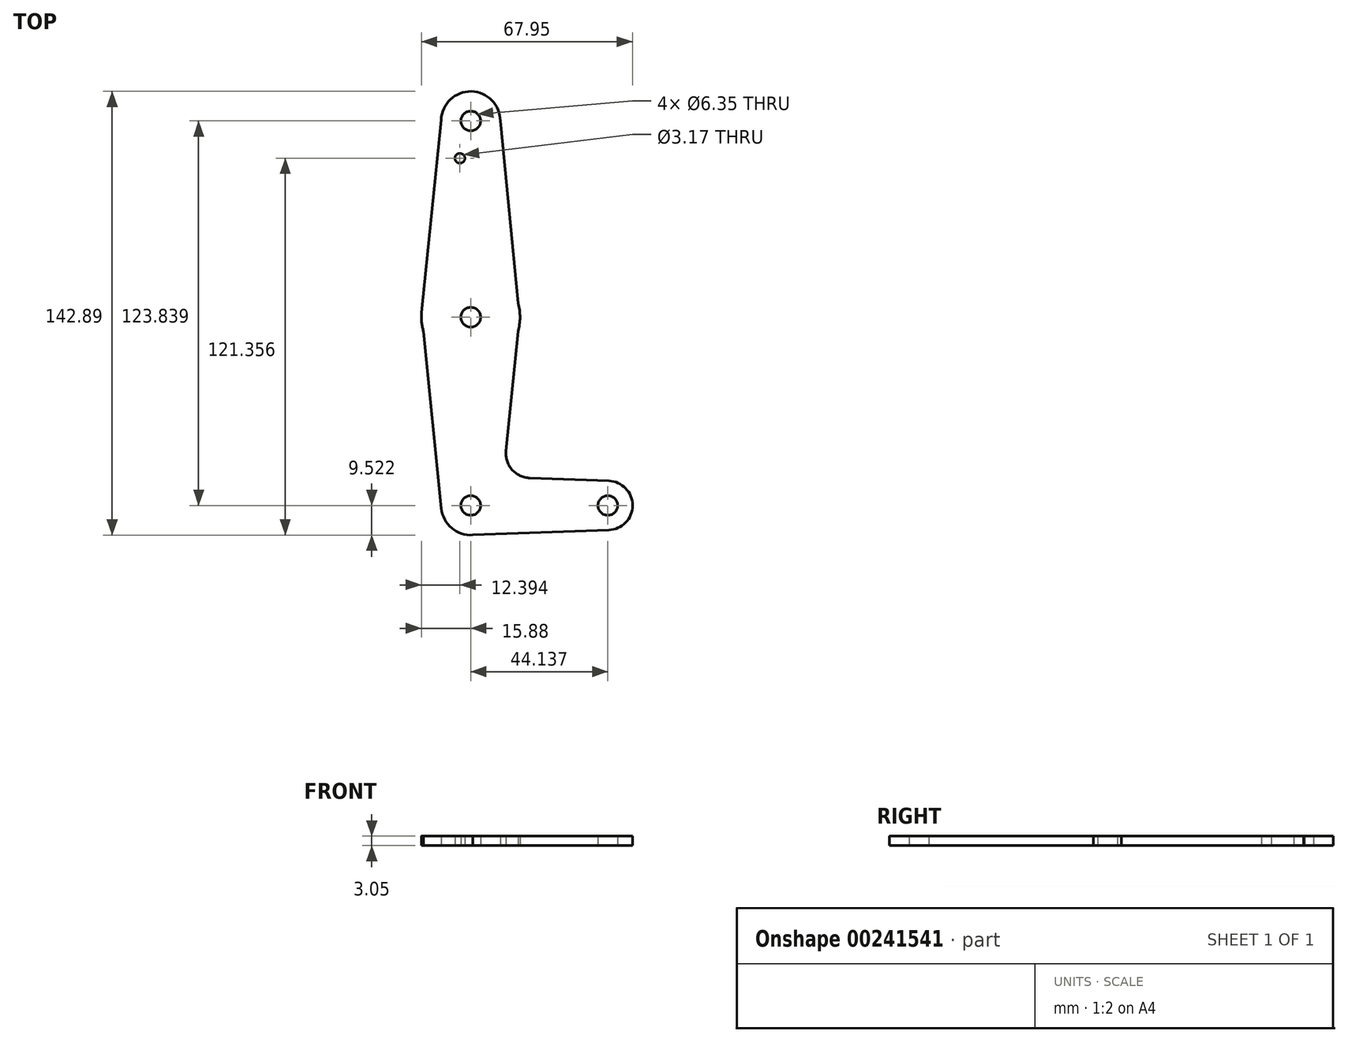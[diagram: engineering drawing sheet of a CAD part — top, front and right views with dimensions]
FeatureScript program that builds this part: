
annotation { "Feature Type Name" : "Feature", "Feature Type Description" : "" }
export const myFeature = defineFeature(function(context is Context, id is Id, definition is map)
    precondition{}
    {
        {
            var Q0;
            Q0=qCreatedBy(makeId("Top.planeOp"),FACE);
            var sketch = newSketch(context, id + "F0", { "sketchPlane" : qUnion([Q0])});
            skCircle(sketch, "E0", {"center": v(0, 0) * mm, "radius": 15.88 * mm});
            skCircle(sketch, "E1", {"center": v(0, 63.2) * mm, "radius": 9.53 * mm});
            skCircle(sketch, "E2", {"center": v(0, -60.64) * mm, "radius": 9.53 * mm});
            skLineSegment(sketch, "E3", {"start": v(-9.4, 64.78) * mm, "end": v(-15.8, 1.6) * mm});
            skLineSegment(sketch, "E4", {"start": v(-15.8, 1.6) * mm, "end": v(-9.48, -61.59) * mm});
            skLineSegment(sketch, "E5", {"start": v(15.67, 0) * mm, "end": v(11.34, -43.05) * mm});
            skLineSegment(sketch, "E6", {"start": v(9.53, 63.2) * mm, "end": v(15.67, 0) * mm});
            skCircle(sketch, "E7", {"center": v(44.14, -60.64) * mm, "radius": 7.94 * mm});
            skLineSegment(sketch, "E8", {"start": v(18.97, -51.8) * mm, "end": v(44.42, -52.7) * mm});
            skLineSegment(sketch, "E9", {"start": v(0, -70.16) * mm, "end": v(44.42, -68.57) * mm});
            skCircle(sketch, "E10", {"center": v(0, 0) * mm, "radius": 3.18 * mm});
            skCircle(sketch, "E11", {"center": v(0, -60.64) * mm, "radius": 3.18 * mm});
            skCircle(sketch, "E12", {"center": v(44.14, -60.64) * mm, "radius": 3.18 * mm});
            skCircle(sketch, "E13", {"center": v(0, 63.2) * mm, "radius": 3.18 * mm});
            skCircle(sketch, "E14", {"center": v(-3.49, 51.2) * mm, "radius": 1.59 * mm});
            skPoint(sketch, "E15.newPointA", {"position": v(9.48, -61.6) * mm});
            skPoint(sketch, "E15.newPointB", {"position": v(0, -51.11) * mm});
            skArc(sketch, "E15.filletArc", {"start": v(11.34, -43.05) * mm, "mid": v(13.26, -49.07) * mm, "end": v(18.97, -51.8) * mm});
            skSolve(sketch);
        }
        {
            var Q0;
            Q0 = qSketchRegion(id + "F0", true);
            extrude(context, id + "F1", {"entities" : qUnion([Q0]), "depth" : 3.05 * mm});
        }
    });
